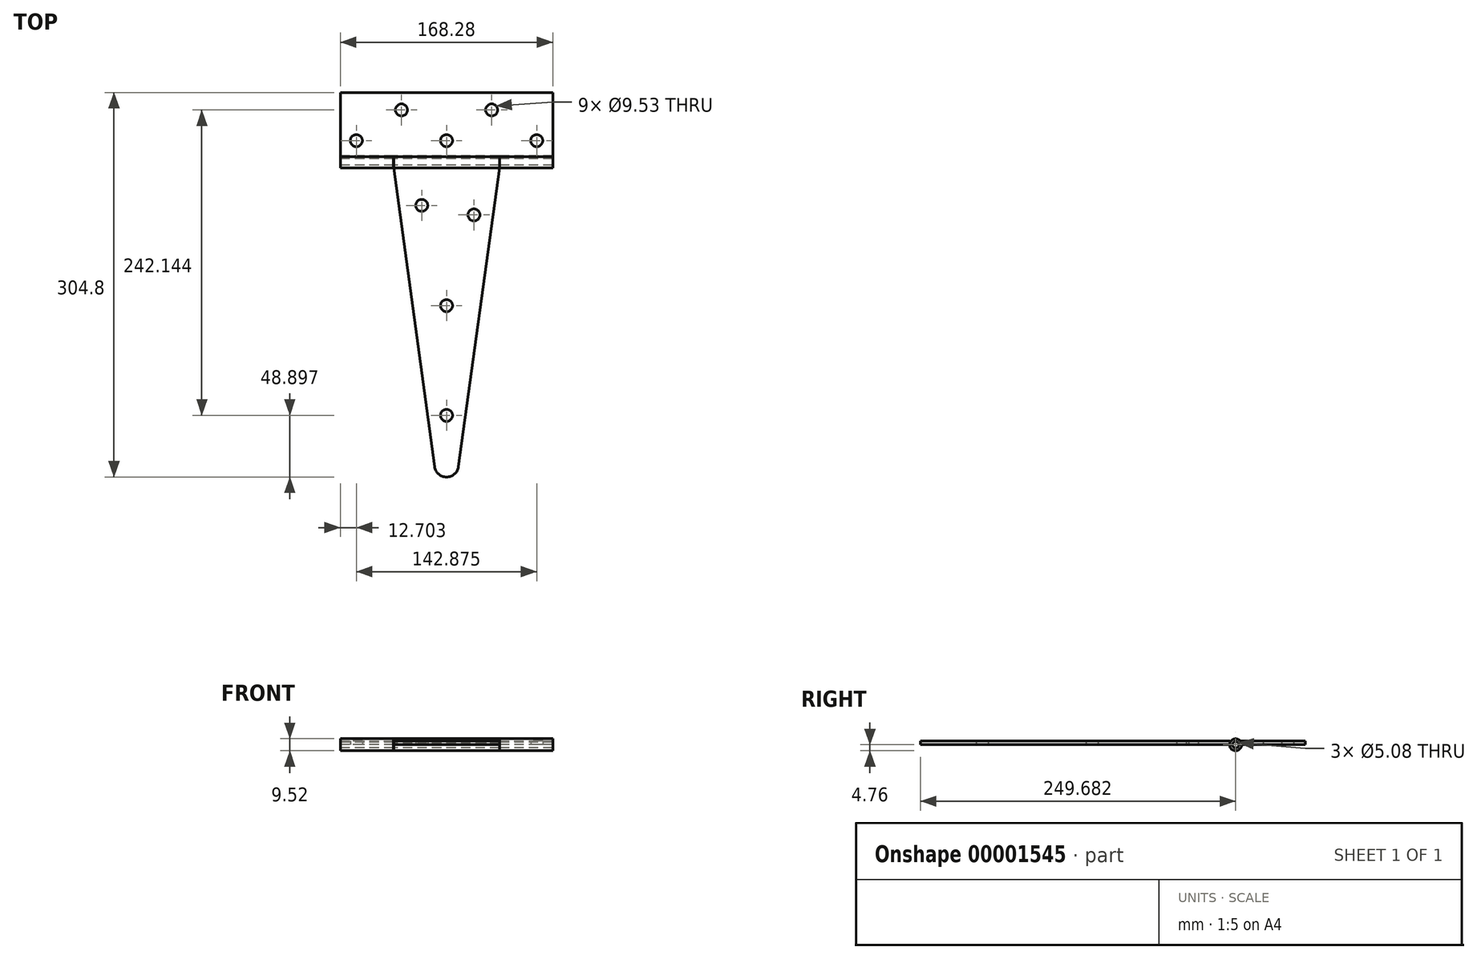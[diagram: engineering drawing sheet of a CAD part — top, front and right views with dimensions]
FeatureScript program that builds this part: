
annotation { "Feature Type Name" : "Feature", "Feature Type Description" : "" }
export const myFeature = defineFeature(function(context is Context, id is Id, definition is map)
    precondition{}
    {
        {
            var Q0;
            Q0=qCreatedBy(makeId("Top.planeOp"),FACE);
            var sketch = newSketch(context, id + "F0", { "sketchPlane" : qUnion([Q0])});
            skLineSegment(sketch, "E0.bottom", {"start": v(-84.14, 25.4) * mm, "end": v(84.14, 25.4) * mm});
            skLineSegment(sketch, "E0.top", {"start": v(-84.14, -25.4) * mm, "end": v(84.14, -25.4) * mm});
            skLineSegment(sketch, "E0.left", {"start": v(-84.14, 25.4) * mm, "end": v(-84.14, -25.4) * mm});
            skLineSegment(sketch, "E0.right", {"start": v(84.14, 25.4) * mm, "end": v(84.14, -25.4) * mm});
            skCircle(sketch, "E1", {"center": v(-71.44, -12.7) * mm, "radius": 4.76 * mm});
            skCircle(sketch, "E2", {"center": v(-35.73, 11.64) * mm, "radius": 4.76 * mm});
            skCircle(sketch, "E3", {"center": v(0, -12.7) * mm, "radius": 4.76 * mm});
            skCircle(sketch, "E4.0.MirrorC", {"center": v(35.73, 11.64) * mm, "radius": 4.76 * mm});
            skCircle(sketch, "E4.1.MirrorC", {"center": v(71.44, -12.7) * mm, "radius": 4.76 * mm});
            skSolve(sketch);
        }
        {
            var Q0;
            Q0=makeQuery(id+"F0.imprint","IMPRINT",FACE,{"disambiguationData":[TD([[makeQuery(id+"F0.imprint","IMPRINT",EDGE,{"derivedFrom":sQuery(id+"F0.wireOp",EDGE,"E0.bottom")}),-1.0]])]});
            extrude(context, id + "F1", {"entities" : qUnion([Q0]), "depth" : 3.1 * mm});
        }
        {
            var Q0;
            Q0=qCreatedBy(makeId("Right.planeOp"),FACE);
            var sketch = newSketch(context, id + "F2", { "sketchPlane" : qUnion([Q0])});
            skCircle(sketch, "E5", {"center": v(-29.72, 0) * mm, "radius": 4.76 * mm});
            skCircle(sketch, "E6", {"center": v(-29.72, 0) * mm, "radius": 2.54 * mm});
            skSolve(sketch);
        }
        {
            var Q0;
            Q0=makeQuery(id+"F2.imprint","IMPRINT",FACE,{"disambiguationData":[TD([[makeQuery(id+"F2.imprint","IMPRINT",EDGE,{"derivedFrom":sQuery(id+"F2.wireOp",EDGE,"E5")}),1.0]])]});
            extrude(context, id + "F3", {"entities" : qUnion([Q0]), "operationType" : NewBodyOperationType.ADD, "endBound" : BoundingType.SYMMETRIC, "depth" : 168.27 * mm});
        }
        {
            var Q0;
            Q0=qCreatedBy(makeId("Right.planeOp"),FACE);
            var sketch = newSketch(context, id + "F4", { "sketchPlane" : qUnion([Q0])});
            skCircle(sketch, "E7", {"center": v(-29.72, 0) * mm, "radius": 4.76 * mm});
            skSolve(sketch);
        }
        {
            var Q0;
            Q0=makeQuery(id+"F4.imprint","IMPRINT",FACE,{"disambiguationData":[TD([[makeQuery(id+"F4.imprint","IMPRINT",EDGE,{"derivedFrom":sQuery(id+"F4.wireOp",EDGE,"E7")}),1.0]])]});
            extrude(context, id + "F5", {"entities" : qUnion([Q0]), "operationType" : NewBodyOperationType.REMOVE, "endBound" : BoundingType.SYMMETRIC, "oppositeDirection" : true, "depth" : 84.14 * mm});
        }
        {
            var Q0;
            Q0=qCreatedBy(makeId("Top.planeOp"),FACE);
            var sketch = newSketch(context, id + "F6", { "sketchPlane" : qUnion([Q0])});
            skLineSegment(sketch, "E8", {"start": v(-41.91, -34.3) * mm, "end": v(41.91, -34.3) * mm});
            skArc(sketch, "E9", {"start": v(-9.44, -271.17) * mm, "mid": v(0, -279.4) * mm, "end": v(9.44, -271.17) * mm});
            skLineSegment(sketch, "E10", {"start": v(41.91, -34.3) * mm, "end": v(9.44, -271.17) * mm});
            skLineSegment(sketch, "E11", {"start": v(-41.91, -34.29) * mm, "end": v(-9.44, -271.17) * mm});
            skCircle(sketch, "E12", {"center": v(0, -230.5) * mm, "radius": 4.76 * mm});
            skCircle(sketch, "E13", {"center": v(0, -143.51) * mm, "radius": 4.76 * mm});
            skCircle(sketch, "E14", {"center": v(21.69, -71.56) * mm, "radius": 4.76 * mm});
            skCircle(sketch, "E15", {"center": v(-19.66, -64.04) * mm, "radius": 4.76 * mm});
            skSolve(sketch);
        }
        {
            var Q0;
            Q0=makeQuery(id+"F6.imprint","IMPRINT",FACE,{"disambiguationData":[TD([[makeQuery(id+"F6.imprint","IMPRINT",EDGE,{"derivedFrom":sQuery(id+"F6.wireOp",EDGE,"E8")}),-1.0]])]});
            extrude(context, id + "F7", {"entities" : qUnion([Q0]), "depth" : 3.1 * mm});
        }
        {
            var Q0;
            Q0=qCreatedBy(makeId("Right.planeOp"),FACE);
            var sketch = newSketch(context, id + "F8", { "sketchPlane" : qUnion([Q0])});
            skCircle(sketch, "E16", {"center": v(-29.72, 0) * mm, "radius": 4.76 * mm});
            skCircle(sketch, "E17", {"center": v(-29.72, 0) * mm, "radius": 2.54 * mm});
            skSolve(sketch);
        }
        {
            var Q0;
            Q0=makeQuery(id+"F8.imprint","IMPRINT",FACE,{"disambiguationData":[TD([[makeQuery(id+"F8.imprint","IMPRINT",EDGE,{"derivedFrom":sQuery(id+"F8.wireOp",EDGE,"E16")}),1.0]])]});
            extrude(context, id + "F9", {"entities" : qUnion([Q0]), "operationType" : NewBodyOperationType.ADD, "endBound" : BoundingType.SYMMETRIC, "depth" : 83.82 * mm});
        }
        {
            var Q0;
            Q0=qCreatedBy(makeId("Right.planeOp"),FACE);
            var sketch = newSketch(context, id + "F10", { "sketchPlane" : qUnion([Q0])});
            skCircle(sketch, "E18", {"center": v(-29.72, 0) * mm, "radius": 2.54 * mm});
            skSolve(sketch);
        }
        {
            var Q0;
            Q0=makeQuery(id+"F10.imprint","IMPRINT",FACE,{"disambiguationData":[TD([[makeQuery(id+"F10.imprint","IMPRINT",EDGE,{"derivedFrom":sQuery(id+"F10.wireOp",EDGE,"E18")}),1.0]])]});
            extrude(context, id + "F11", {"entities" : qUnion([Q0]), "endBound" : BoundingType.SYMMETRIC, "depth" : 168.27 * mm});
        }
    });
